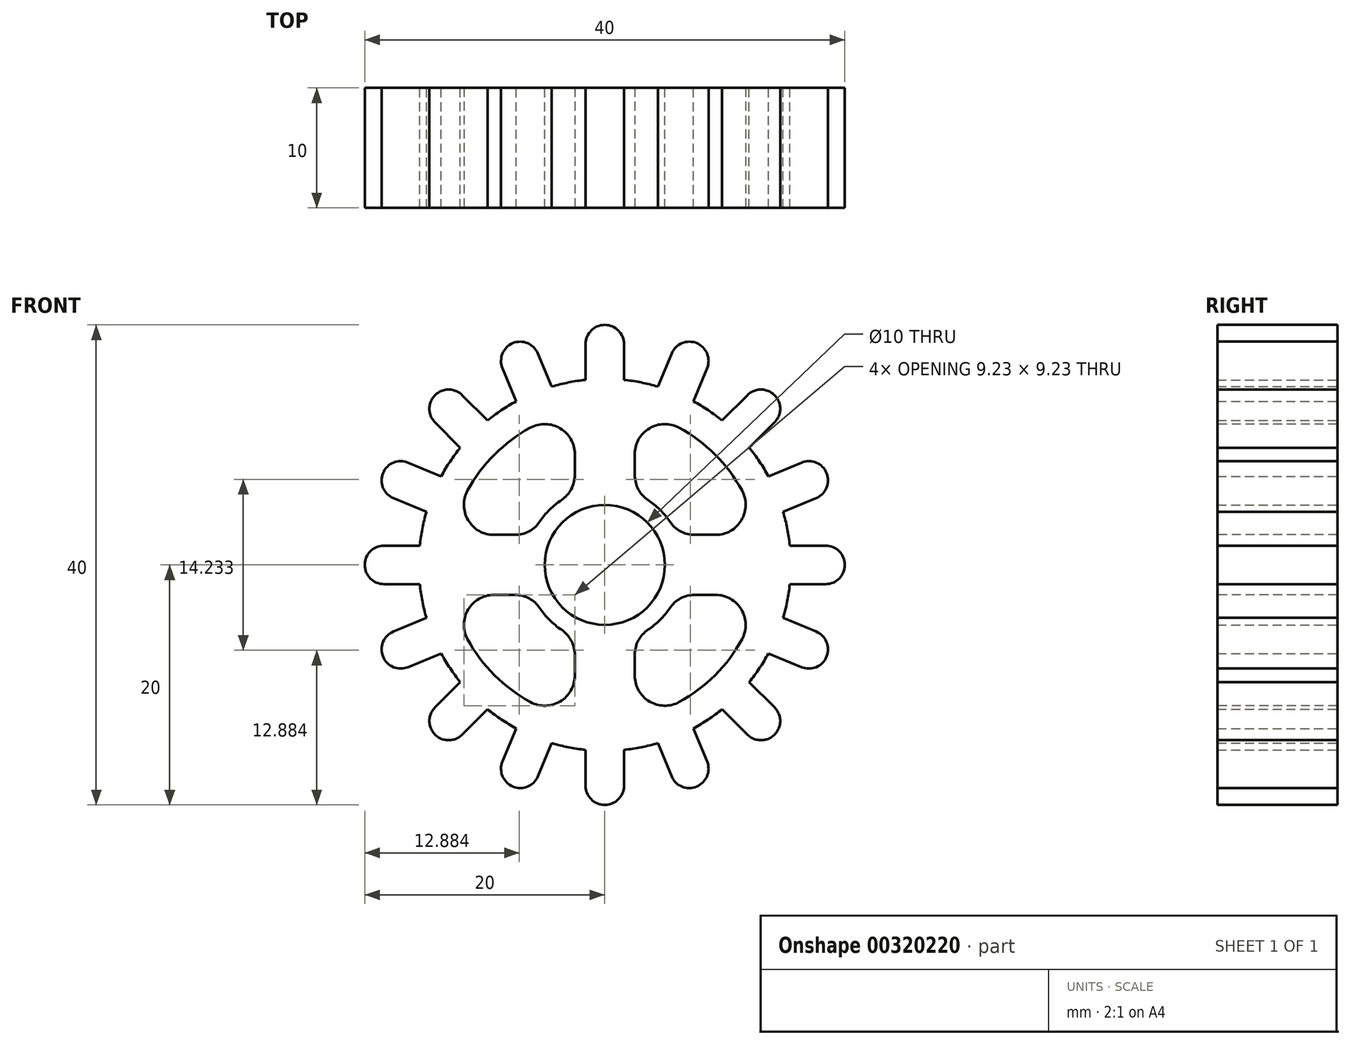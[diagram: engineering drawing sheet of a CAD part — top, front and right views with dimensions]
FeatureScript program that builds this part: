
annotation { "Feature Type Name" : "Feature", "Feature Type Description" : "" }
export const myFeature = defineFeature(function(context is Context, id is Id, definition is map)
    precondition{}
    {
        {
            var Q0;
            Q0=qCreatedBy(makeId("Front.planeOp"),FACE);
            var sketch = newSketch(context, id + "F0", { "sketchPlane" : qUnion([Q0])});
            skCircle(sketch, "E0", {"center": v(0, 0) * mm, "radius": 5 * mm});
            skArc(sketch, "E1", {"start": v(-7.38, 13.63) * mm, "mid": v(-8.61, 12.89) * mm, "end": v(-9.77, 12.03) * mm});
            skArc(sketch, "E2", {"start": v(1.6, 18.4) * mm, "mid": v(0, 20) * mm, "end": v(-1.6, 18.4) * mm});
            skLineSegment(sketch, "E3", {"start": v(1.6, 18.4) * mm, "end": v(1.6, 15.42) * mm});
            skLineSegment(sketch, "E4", {"start": v(-1.6, 18.4) * mm, "end": v(-1.6, 15.42) * mm});
            skLineSegment(sketch, "E5.1.0", {"start": v(-5.56, 17.61) * mm, "end": v(-4.42, 14.86) * mm});
            skArc(sketch, "E5.1.1", {"start": v(-5.56, 17.61) * mm, "mid": v(-7.65, 18.48) * mm, "end": v(-8.52, 16.39) * mm});
            skLineSegment(sketch, "E5.1.2", {"start": v(-8.52, 16.39) * mm, "end": v(-7.38, 13.63) * mm});
            skLineSegment(sketch, "E5.2.0", {"start": v(-11.88, 14.14) * mm, "end": v(-9.77, 12.03) * mm});
            skArc(sketch, "E5.2.1", {"start": v(-11.88, 14.14) * mm, "mid": v(-14.14, 14.14) * mm, "end": v(-14.14, 11.88) * mm});
            skLineSegment(sketch, "E5.2.2", {"start": v(-14.14, 11.88) * mm, "end": v(-12.03, 9.77) * mm});
            skLineSegment(sketch, "E5.3.0", {"start": v(-16.39, 8.52) * mm, "end": v(-13.63, 7.38) * mm});
            skArc(sketch, "E5.3.1", {"start": v(-16.39, 8.52) * mm, "mid": v(-18.48, 7.65) * mm, "end": v(-17.61, 5.56) * mm});
            skLineSegment(sketch, "E5.3.2", {"start": v(-17.61, 5.56) * mm, "end": v(-14.86, 4.42) * mm});
            skLineSegment(sketch, "E5.4.0", {"start": v(-18.4, 1.6) * mm, "end": v(-15.42, 1.6) * mm});
            skArc(sketch, "E5.4.1", {"start": v(-18.4, 1.6) * mm, "mid": v(-20, 0) * mm, "end": v(-18.4, -1.6) * mm});
            skLineSegment(sketch, "E5.4.2", {"start": v(-18.4, -1.6) * mm, "end": v(-15.42, -1.6) * mm});
            skLineSegment(sketch, "E5.5.0", {"start": v(-17.61, -5.56) * mm, "end": v(-14.86, -4.42) * mm});
            skArc(sketch, "E5.5.1", {"start": v(-17.61, -5.56) * mm, "mid": v(-18.48, -7.65) * mm, "end": v(-16.39, -8.52) * mm});
            skLineSegment(sketch, "E5.5.2", {"start": v(-16.39, -8.52) * mm, "end": v(-13.63, -7.38) * mm});
            skLineSegment(sketch, "E5.6.0", {"start": v(-14.14, -11.88) * mm, "end": v(-12.03, -9.77) * mm});
            skArc(sketch, "E5.6.1", {"start": v(-14.14, -11.88) * mm, "mid": v(-14.14, -14.14) * mm, "end": v(-11.88, -14.14) * mm});
            skLineSegment(sketch, "E5.6.2", {"start": v(-11.88, -14.14) * mm, "end": v(-9.77, -12.03) * mm});
            skLineSegment(sketch, "E5.7.0", {"start": v(-8.52, -16.39) * mm, "end": v(-7.38, -13.63) * mm});
            skArc(sketch, "E5.7.1", {"start": v(-8.52, -16.39) * mm, "mid": v(-7.65, -18.48) * mm, "end": v(-5.56, -17.61) * mm});
            skLineSegment(sketch, "E5.7.2", {"start": v(-5.56, -17.61) * mm, "end": v(-4.42, -14.86) * mm});
            skLineSegment(sketch, "E5.8.0", {"start": v(-1.6, -18.4) * mm, "end": v(-1.6, -15.42) * mm});
            skArc(sketch, "E5.8.1", {"start": v(-1.6, -18.4) * mm, "mid": v(0, -20) * mm, "end": v(1.6, -18.4) * mm});
            skLineSegment(sketch, "E5.8.2", {"start": v(1.6, -18.4) * mm, "end": v(1.6, -15.42) * mm});
            skLineSegment(sketch, "E5.9.0", {"start": v(5.56, -17.61) * mm, "end": v(4.42, -14.86) * mm});
            skArc(sketch, "E5.9.1", {"start": v(5.56, -17.61) * mm, "mid": v(7.65, -18.48) * mm, "end": v(8.52, -16.39) * mm});
            skLineSegment(sketch, "E5.9.2", {"start": v(8.52, -16.39) * mm, "end": v(7.38, -13.63) * mm});
            skLineSegment(sketch, "E5.10.0", {"start": v(11.88, -14.14) * mm, "end": v(9.77, -12.03) * mm});
            skArc(sketch, "E5.10.1", {"start": v(11.88, -14.14) * mm, "mid": v(14.14, -14.14) * mm, "end": v(14.14, -11.88) * mm});
            skLineSegment(sketch, "E5.10.2", {"start": v(14.14, -11.88) * mm, "end": v(12.03, -9.77) * mm});
            skLineSegment(sketch, "E5.11.0", {"start": v(16.39, -8.52) * mm, "end": v(13.63, -7.38) * mm});
            skArc(sketch, "E5.11.1", {"start": v(16.39, -8.52) * mm, "mid": v(18.48, -7.65) * mm, "end": v(17.61, -5.56) * mm});
            skLineSegment(sketch, "E5.11.2", {"start": v(17.61, -5.56) * mm, "end": v(14.86, -4.42) * mm});
            skLineSegment(sketch, "E5.12.0", {"start": v(18.4, -1.6) * mm, "end": v(15.42, -1.6) * mm});
            skArc(sketch, "E5.12.1", {"start": v(18.4, -1.6) * mm, "mid": v(20, 0) * mm, "end": v(18.4, 1.6) * mm});
            skLineSegment(sketch, "E5.12.2", {"start": v(18.4, 1.6) * mm, "end": v(15.42, 1.6) * mm});
            skLineSegment(sketch, "E5.13.0", {"start": v(17.61, 5.56) * mm, "end": v(14.86, 4.42) * mm});
            skArc(sketch, "E5.13.1", {"start": v(17.61, 5.56) * mm, "mid": v(18.48, 7.65) * mm, "end": v(16.39, 8.52) * mm});
            skLineSegment(sketch, "E5.13.2", {"start": v(16.39, 8.52) * mm, "end": v(13.63, 7.38) * mm});
            skLineSegment(sketch, "E5.14.0", {"start": v(14.14, 11.88) * mm, "end": v(12.03, 9.77) * mm});
            skArc(sketch, "E5.14.1", {"start": v(14.14, 11.88) * mm, "mid": v(14.14, 14.14) * mm, "end": v(11.88, 14.14) * mm});
            skLineSegment(sketch, "E5.14.2", {"start": v(11.88, 14.14) * mm, "end": v(9.77, 12.03) * mm});
            skArc(sketch, "E6.trimOffspring", {"start": v(-12.03, 9.77) * mm, "mid": v(-12.89, 8.61) * mm, "end": v(-13.63, 7.38) * mm});
            skArc(sketch, "E7.trimOffspring", {"start": v(-14.86, 4.42) * mm, "mid": v(-15.2, 3.02) * mm, "end": v(-15.42, 1.6) * mm});
            skArc(sketch, "E8.trimOffspring", {"start": v(-15.42, -1.6) * mm, "mid": v(-15.2, -3.02) * mm, "end": v(-14.86, -4.42) * mm});
            skArc(sketch, "E9.trimOffspring", {"start": v(-13.63, -7.38) * mm, "mid": v(-12.89, -8.61) * mm, "end": v(-12.03, -9.77) * mm});
            skArc(sketch, "E10.trimOffspring", {"start": v(-9.77, -12.03) * mm, "mid": v(-8.61, -12.89) * mm, "end": v(-7.38, -13.63) * mm});
            skArc(sketch, "E11.trimOffspring", {"start": v(-4.42, -14.86) * mm, "mid": v(-3.02, -15.2) * mm, "end": v(-1.6, -15.42) * mm});
            skArc(sketch, "E12.trimOffspring", {"start": v(1.6, -15.42) * mm, "mid": v(3.02, -15.2) * mm, "end": v(4.42, -14.86) * mm});
            skArc(sketch, "E13.trimOffspring", {"start": v(7.38, -13.63) * mm, "mid": v(8.61, -12.89) * mm, "end": v(9.77, -12.03) * mm});
            skArc(sketch, "E14.trimOffspring", {"start": v(12.03, -9.77) * mm, "mid": v(12.89, -8.61) * mm, "end": v(13.63, -7.38) * mm});
            skArc(sketch, "E15.trimOffspring", {"start": v(14.86, -4.42) * mm, "mid": v(15.2, -3.02) * mm, "end": v(15.42, -1.6) * mm});
            skArc(sketch, "E16.trimOffspring", {"start": v(15.42, 1.6) * mm, "mid": v(15.2, 3.02) * mm, "end": v(14.86, 4.42) * mm});
            skArc(sketch, "E17.trimOffspring", {"start": v(13.63, 7.38) * mm, "mid": v(10.96, 10.96) * mm, "end": v(7.38, 13.63) * mm});
            skArc(sketch, "E18.trimOffspring", {"start": v(4.42, 14.86) * mm, "mid": v(3.02, 15.2) * mm, "end": v(1.6, 15.42) * mm});
            skArc(sketch, "E19.trimOffspring", {"start": v(-1.6, 15.42) * mm, "mid": v(-3.02, 15.2) * mm, "end": v(-4.42, 14.86) * mm});
            skLineSegment(sketch, "E20.2.15.0", {"start": v(8.52, 16.39) * mm, "end": v(7.38, 13.63) * mm});
            skArc(sketch, "E20.3.15.0", {"start": v(8.52, 16.39) * mm, "mid": v(7.65, 18.48) * mm, "end": v(5.56, 17.61) * mm});
            skLineSegment(sketch, "E20.7.15.0", {"start": v(5.56, 17.61) * mm, "end": v(4.42, 14.86) * mm});
            skSolve(sketch);
        }
        {
            var Q0;
            Q0=qSketchRegion(id+"F0",true);
            extrude(context, id + "F1", {"entities" : qUnion([Q0]), "endBound" : BoundingType.SYMMETRIC, "depth" : 10 * mm});
        }
        {
            var Q0;
            Q0=makeQuery(id+"F1.opExtrude","CAP_FACE",FACE,{"disambiguationData":[OSD([sQuery(id+"F0.wireOp",EDGE,"E0"),sQuery(id+"F0.wireOp",EDGE,"E1"),sQuery(id+"F0.wireOp",EDGE,"E2"),sQuery(id+"F0.wireOp",EDGE,"E3"),sQuery(id+"F0.wireOp",EDGE,"E4"),sQuery(id+"F0.wireOp",EDGE,"E5.1.0"),sQuery(id+"F0.wireOp",EDGE,"E5.1.1"),sQuery(id+"F0.wireOp",EDGE,"E5.1.2"),sQuery(id+"F0.wireOp",EDGE,"E5.2.0"),sQuery(id+"F0.wireOp",EDGE,"E5.2.1"),sQuery(id+"F0.wireOp",EDGE,"E5.2.2"),sQuery(id+"F0.wireOp",EDGE,"E5.3.0"),sQuery(id+"F0.wireOp",EDGE,"E5.3.1"),sQuery(id+"F0.wireOp",EDGE,"E5.3.2"),sQuery(id+"F0.wireOp",EDGE,"E5.4.0"),sQuery(id+"F0.wireOp",EDGE,"E5.4.1"),sQuery(id+"F0.wireOp",EDGE,"E5.4.2"),sQuery(id+"F0.wireOp",EDGE,"E5.5.0"),sQuery(id+"F0.wireOp",EDGE,"E5.5.1"),sQuery(id+"F0.wireOp",EDGE,"E5.5.2"),sQuery(id+"F0.wireOp",EDGE,"E5.6.0"),sQuery(id+"F0.wireOp",EDGE,"E5.6.1"),sQuery(id+"F0.wireOp",EDGE,"E5.6.2"),sQuery(id+"F0.wireOp",EDGE,"E5.7.0"),sQuery(id+"F0.wireOp",EDGE,"E5.7.1"),sQuery(id+"F0.wireOp",EDGE,"E5.7.2"),sQuery(id+"F0.wireOp",EDGE,"E5.8.0"),sQuery(id+"F0.wireOp",EDGE,"E5.8.1"),sQuery(id+"F0.wireOp",EDGE,"E5.8.2"),sQuery(id+"F0.wireOp",EDGE,"E5.9.0"),sQuery(id+"F0.wireOp",EDGE,"E5.9.1"),sQuery(id+"F0.wireOp",EDGE,"E5.9.2"),sQuery(id+"F0.wireOp",EDGE,"E5.10.0"),sQuery(id+"F0.wireOp",EDGE,"E5.10.1"),sQuery(id+"F0.wireOp",EDGE,"E5.10.2"),sQuery(id+"F0.wireOp",EDGE,"E5.11.0"),sQuery(id+"F0.wireOp",EDGE,"E5.11.1"),sQuery(id+"F0.wireOp",EDGE,"E5.11.2"),sQuery(id+"F0.wireOp",EDGE,"E5.12.0"),sQuery(id+"F0.wireOp",EDGE,"E5.12.1"),sQuery(id+"F0.wireOp",EDGE,"E5.12.2"),sQuery(id+"F0.wireOp",EDGE,"E5.13.0"),sQuery(id+"F0.wireOp",EDGE,"E5.13.1"),sQuery(id+"F0.wireOp",EDGE,"E5.13.2"),sQuery(id+"F0.wireOp",EDGE,"E5.14.0"),sQuery(id+"F0.wireOp",EDGE,"E5.14.1"),sQuery(id+"F0.wireOp",EDGE,"E5.14.2"),sQuery(id+"F0.wireOp",EDGE,"E6.trimOffspring"),sQuery(id+"F0.wireOp",EDGE,"E7.trimOffspring"),sQuery(id+"F0.wireOp",EDGE,"E8.trimOffspring"),sQuery(id+"F0.wireOp",EDGE,"E9.trimOffspring"),sQuery(id+"F0.wireOp",EDGE,"E10.trimOffspring"),sQuery(id+"F0.wireOp",EDGE,"E11.trimOffspring"),sQuery(id+"F0.wireOp",EDGE,"E12.trimOffspring"),sQuery(id+"F0.wireOp",EDGE,"E13.trimOffspring"),sQuery(id+"F0.wireOp",EDGE,"E14.trimOffspring"),sQuery(id+"F0.wireOp",EDGE,"E15.trimOffspring"),sQuery(id+"F0.wireOp",EDGE,"E16.trimOffspring"),sQuery(id+"F0.wireOp",EDGE,"E17.trimOffspring"),sQuery(id+"F0.wireOp",EDGE,"E18.trimOffspring"),sQuery(id+"F0.wireOp",EDGE,"E19.trimOffspring")])],"isStart":false});
            var sketch = newSketch(context, id + "F2", { "sketchPlane" : qUnion([Q0])});
            skArc(sketch, "E21", {"start": v(-11.43, 6.2) * mm, "mid": v(-9.2, 9.2) * mm, "end": v(-6.2, 11.43) * mm});
            skLineSegment(sketch, "E22", {"start": v(0, 0) * mm, "end": v(0, 23.63) * mm, "construction": true});
            skLineSegment(sketch, "E23", {"start": v(0, 23.63) * mm, "end": v(0, 13) * mm, "construction": true});
            skLineSegment(sketch, "E24", {"start": v(0, 0) * mm, "end": v(-36.4, 0) * mm, "construction": true});
            skLineSegment(sketch, "E25", {"start": v(-2.5, 9.23) * mm, "end": v(-2.5, 7.48) * mm});
            skLineSegment(sketch, "E26", {"start": v(-9.23, 2.5) * mm, "end": v(-7.48, 2.5) * mm});
            skArc(sketch, "E27.trimOffspring", {"start": v(-3.61, 5.4) * mm, "mid": v(-4.6, 4.6) * mm, "end": v(-5.4, 3.61) * mm});
            skPoint(sketch, "E28.orphan", {"position": v(0, 13) * mm});
            skPoint(sketch, "E29.orphan", {"position": v(-13, 0) * mm});
            skPoint(sketch, "E30.visualSharp", {"position": v(-2.5, 12.76) * mm});
            skArc(sketch, "E30.filletArc", {"start": v(-2.5, 9.23) * mm, "mid": v(-3.72, 11.38) * mm, "end": v(-6.2, 11.43) * mm});
            skPoint(sketch, "E31.visualSharp", {"position": v(-12.76, 2.5) * mm});
            skArc(sketch, "E31.filletArc", {"start": v(-11.43, 6.2) * mm, "mid": v(-11.38, 3.72) * mm, "end": v(-9.23, 2.5) * mm});
            skPoint(sketch, "E32.visualSharp", {"position": v(-6, 2.5) * mm});
            skArc(sketch, "E32.filletArc", {"start": v(-7.48, 2.5) * mm, "mid": v(-6.3, 2.8) * mm, "end": v(-5.4, 3.61) * mm});
            skPoint(sketch, "E33.visualSharp", {"position": v(-2.5, 6) * mm});
            skArc(sketch, "E33.filletArc", {"start": v(-3.61, 5.4) * mm, "mid": v(-2.8, 6.3) * mm, "end": v(-2.5, 7.48) * mm});
            skArc(sketch, "E34.MirrorCS", {"start": v(2.5, 9.23) * mm, "mid": v(3.72, 11.38) * mm, "end": v(6.2, 11.43) * mm});
            skArc(sketch, "E35.MirrorCS", {"start": v(11.43, 6.2) * mm, "mid": v(9.2, 9.2) * mm, "end": v(6.2, 11.43) * mm});
            skArc(sketch, "E36.MirrorCS", {"start": v(11.43, 6.2) * mm, "mid": v(11.38, 3.72) * mm, "end": v(9.23, 2.5) * mm});
            skLineSegment(sketch, "E37.MirrorCS", {"start": v(9.23, 2.5) * mm, "end": v(7.48, 2.5) * mm});
            skArc(sketch, "E38.MirrorCS", {"start": v(7.48, 2.5) * mm, "mid": v(6.3, 2.8) * mm, "end": v(5.4, 3.61) * mm});
            skArc(sketch, "E39.MirrorCS", {"start": v(3.61, 5.4) * mm, "mid": v(4.6, 4.6) * mm, "end": v(5.4, 3.61) * mm});
            skArc(sketch, "E40.MirrorCS", {"start": v(3.61, 5.4) * mm, "mid": v(2.8, 6.3) * mm, "end": v(2.5, 7.48) * mm});
            skLineSegment(sketch, "E41.MirrorCS", {"start": v(2.5, 9.23) * mm, "end": v(2.5, 7.48) * mm});
            skLineSegment(sketch, "E42.0", {"start": v(0, 5) * mm, "end": v(-11.73, 5) * mm});
            skLineSegment(sketch, "E43.MirrorCS", {"start": v(-9.23, -2.5) * mm, "end": v(-7.48, -2.5) * mm});
            skArc(sketch, "E44.MirrorCS", {"start": v(-11.43, -6.2) * mm, "mid": v(-11.38, -3.72) * mm, "end": v(-9.23, -2.5) * mm});
            skArc(sketch, "E45.MirrorCS", {"start": v(-11.43, -6.2) * mm, "mid": v(-9.2, -9.2) * mm, "end": v(-6.2, -11.43) * mm});
            skArc(sketch, "E46.MirrorCS", {"start": v(-2.5, -9.23) * mm, "mid": v(-3.72, -11.38) * mm, "end": v(-6.2, -11.43) * mm});
            skLineSegment(sketch, "E47.MirrorCS", {"start": v(-2.5, -9.23) * mm, "end": v(-2.5, -7.48) * mm});
            skPoint(sketch, "E48.MirrorP", {"position": v(-2.5, -6) * mm});
            skArc(sketch, "E49.MirrorCS", {"start": v(-3.61, -5.4) * mm, "mid": v(-4.6, -4.6) * mm, "end": v(-5.4, -3.61) * mm});
            skArc(sketch, "E50.MirrorCS", {"start": v(-3.61, -5.4) * mm, "mid": v(-2.8, -6.3) * mm, "end": v(-2.5, -7.48) * mm});
            skArc(sketch, "E51.MirrorCS", {"start": v(-7.48, -2.5) * mm, "mid": v(-6.3, -2.8) * mm, "end": v(-5.4, -3.61) * mm});
            skArc(sketch, "E52.MirrorCS", {"start": v(3.61, -5.4) * mm, "mid": v(2.8, -6.3) * mm, "end": v(2.5, -7.48) * mm});
            skLineSegment(sketch, "E53.MirrorCS", {"start": v(2.5, -9.23) * mm, "end": v(2.5, -7.48) * mm});
            skArc(sketch, "E54.MirrorCS", {"start": v(2.5, -9.23) * mm, "mid": v(3.72, -11.38) * mm, "end": v(6.2, -11.43) * mm});
            skArc(sketch, "E55.MirrorCS", {"start": v(11.43, -6.2) * mm, "mid": v(9.2, -9.2) * mm, "end": v(6.2, -11.43) * mm});
            skArc(sketch, "E56.MirrorCS", {"start": v(11.43, -6.2) * mm, "mid": v(11.38, -3.72) * mm, "end": v(9.23, -2.5) * mm});
            skLineSegment(sketch, "E57.MirrorCS", {"start": v(9.23, -2.5) * mm, "end": v(7.48, -2.5) * mm});
            skArc(sketch, "E58.MirrorCS", {"start": v(7.48, -2.5) * mm, "mid": v(6.3, -2.8) * mm, "end": v(5.4, -3.61) * mm});
            skArc(sketch, "E59.MirrorCS", {"start": v(3.61, -5.4) * mm, "mid": v(4.6, -4.6) * mm, "end": v(5.4, -3.61) * mm});
            skLineSegment(sketch, "E60.trimOffspring", {"start": v(0, 5) * mm, "end": v(0, 0) * mm, "construction": true});
            skSolve(sketch);
        }
        {
            var Q0;
            Q0=qSketchRegion(id+"F2",true);
            extrude(context, id + "F3", {"entities" : qUnion([Q0]), "operationType" : NewBodyOperationType.REMOVE, "oppositeDirection" : true, "depth" : 10 * mm});
        }
    });
